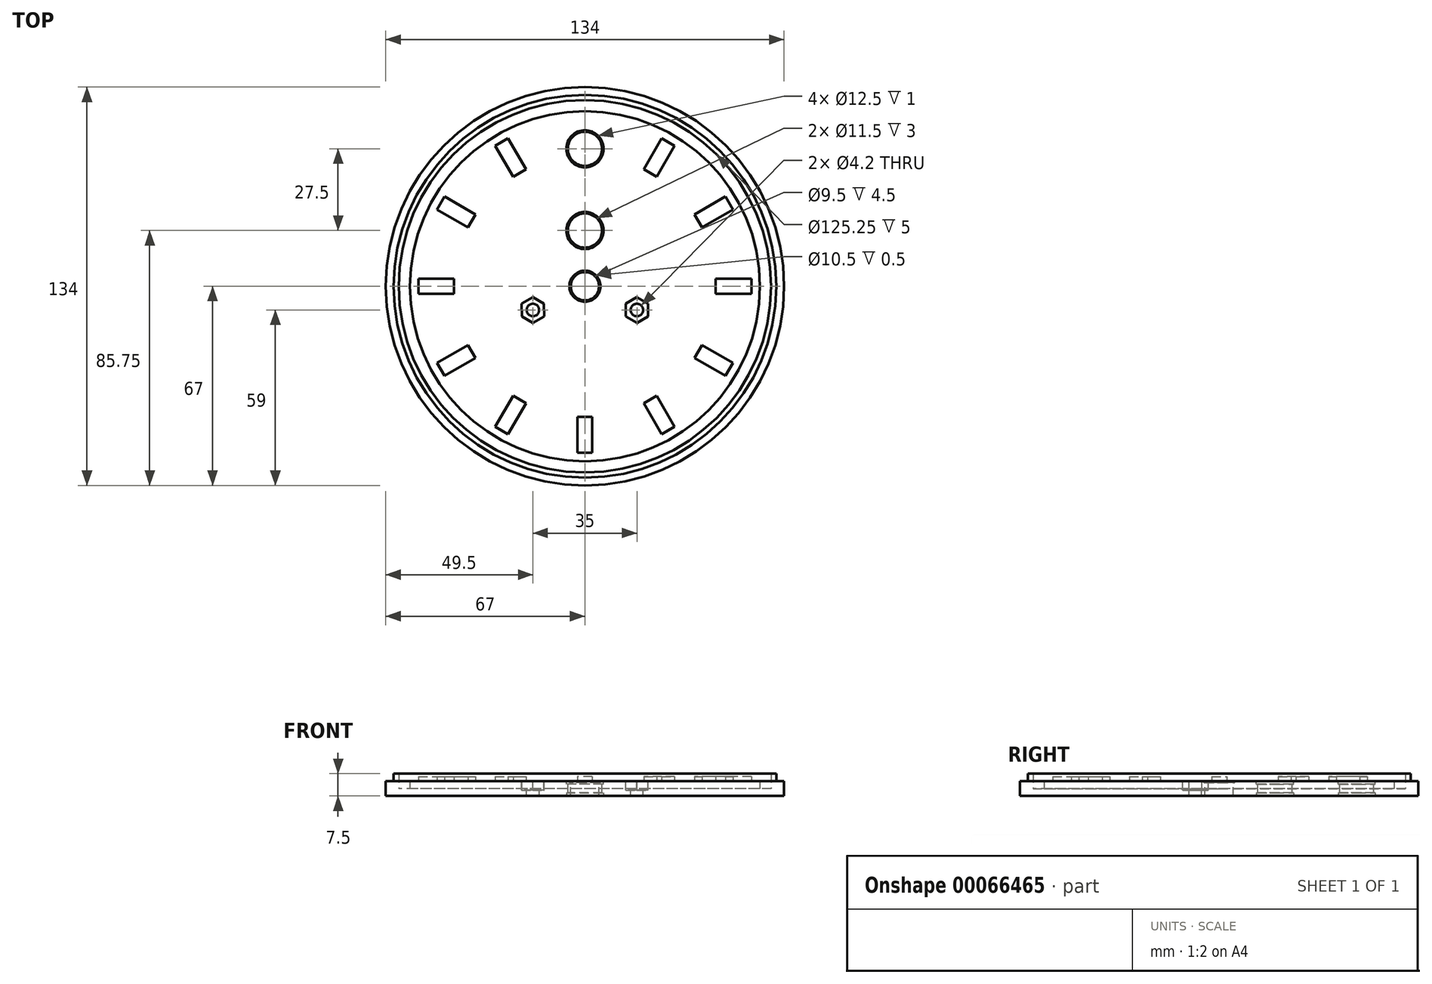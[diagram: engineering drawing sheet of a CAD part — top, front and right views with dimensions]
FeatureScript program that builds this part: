
annotation { "Feature Type Name" : "Feature", "Feature Type Description" : "" }
export const myFeature = defineFeature(function(context is Context, id is Id, definition is map)
    precondition{}
    {
        {
            var Q0;
            Q0=qCreatedBy(makeId("Top.planeOp"),FACE);
            var sketch = newSketch(context, id + "F0", { "sketchPlane" : qUnion([Q0])});
            skCircle(sketch, "E0", {"center": v(0, 0) * mm, "radius": 67 * mm});
            skSolve(sketch);
        }
        {
            var Q0;
            Q0 = qSketchRegion(id + "F0", true);
            extrude(context, id + "F1", {"entities" : qUnion([Q0]), "endBound" : BoundingType.SYMMETRIC, "depth" : 5 * mm});
        }
        {
            var Q0;
            Q0=qCreatedBy(makeId("Top.planeOp"),FACE);
            var sketch = newSketch(context, id + "F2", { "sketchPlane" : qUnion([Q0])});
            skCircle(sketch, "E1", {"center": v(0, 0) * mm, "radius": 64.38 * mm});
            skCircle(sketch, "E2", {"center": v(0, 0) * mm, "radius": 62.62 * mm});
            skCircle(sketch, "E3", {"center": v(0, 0) * mm, "radius": 58.88 * mm});
            skSolve(sketch);
        }
        {
            var Q0;
            Q0 = qSketchRegion(id + "F2", true);
            extrude(context, id + "F3", {"entities" : qUnion([Q0]), "operationType" : NewBodyOperationType.ADD, "depth" : 5 * mm});
        }
        {
            var Q0;
            Q0=qCreatedBy(makeId("Top.planeOp"),FACE);
            var sketch = newSketch(context, id + "F4", { "sketchPlane" : qUnion([Q0])});
            skCircle(sketch, "E4", {"center": v(0, 0) * mm, "radius": 58.88 * mm});
            skCircle(sketch, "E5", {"center": v(0, 0) * mm, "radius": 62.62 * mm});
            skSolve(sketch);
        }
        {
            var Q0;
            Q0 = qSketchRegion(id + "F4", true);
            extrude(context, id + "F5", {"entities" : qUnion([Q0]), "operationType" : NewBodyOperationType.REMOVE, "depth" : 5 * mm});
        }
        {
            var Q0;
            Q0=makeQuery(id+"F3.boolean.opBoolean","SPLIT",FACE,{"disambiguationData":[TD([makeQuery(id+"F3.opExtrude","SWEPT_FACE",FACE,{"disambiguationData":[OSD([sQuery(id+"F2.wireOp",EDGE,"E2")])]})])],"derivedFrom":makeQuery(id+"F1.opExtrude","CAP_FACE",FACE,{"disambiguationData":[OSD([sQuery(id+"F0.wireOp",EDGE,"E0")])],"isStart":false})});
            var sketch = newSketch(context, id + "F6", { "sketchPlane" : qUnion([Q0])});
            skCircle(sketch, "E6", {"center": v(0, 0) * mm, "radius": 4.75 * mm});
            skCircle(sketch, "E7", {"center": v(0, 18.75) * mm, "radius": 5.75 * mm});
            skCircle(sketch, "E8", {"center": v(0, 46.25) * mm, "radius": 5.75 * mm});
            skLineSegment(sketch, "E9", {"start": v(0, -8) * mm, "end": v(17.5, -8) * mm, "construction": true});
            skLineSegment(sketch, "E10", {"start": v(0, 0) * mm, "end": v(0, -8) * mm, "construction": true});
            skCircle(sketch, "E11", {"center": v(17.5, -8) * mm, "radius": 2.1 * mm});
            skCircle(sketch, "E12.MirrorC", {"center": v(-17.5, -8) * mm, "radius": 2.1 * mm});
            skSolve(sketch);
        }
        {
            var Q0;
            Q0 = qSketchRegion(id + "F6", true);
            extrude(context, id + "F7", {"entities" : qUnion([Q0]), "operationType" : NewBodyOperationType.REMOVE, "endBound" : BoundingType.THROUGH_ALL, "oppositeDirection" : true, "depth" : 25 * mm});
        }
        {
            var Q0;
            Q0=makeQuery(id+"F3.boolean.opBoolean","SPLIT",FACE,{"disambiguationData":[TD([makeQuery(id+"F3.opExtrude","SWEPT_FACE",FACE,{"disambiguationData":[OSD([sQuery(id+"F2.wireOp",EDGE,"E2")])]})])],"derivedFrom":makeQuery(id+"F1.opExtrude","CAP_FACE",FACE,{"disambiguationData":[OSD([sQuery(id+"F0.wireOp",EDGE,"E0")])],"isStart":false})});
            var sketch = newSketch(context, id + "F8", { "sketchPlane" : qUnion([Q0])});
            skCircle(sketch, "E13", {"center": v(0, 46.25) * mm, "radius": 6.25 * mm});
            skCircle(sketch, "E14", {"center": v(0, 18.75) * mm, "radius": 6.25 * mm});
            skCircle(sketch, "E15", {"center": v(0, 0) * mm, "radius": 5.25 * mm});
            skCircle(sketch, "E16.cCircle", {"center": v(17.5, -8) * mm, "radius": 3.75 * mm, "construction": true});
            skLineSegment(sketch, "E16.0", {"start": v(21.27, -10.14) * mm, "end": v(17.53, -12.33) * mm});
            skLineSegment(sketch, "E16.1", {"start": v(17.53, -12.33) * mm, "end": v(13.77, -10.2) * mm});
            skLineSegment(sketch, "E16.2", {"start": v(13.77, -10.2) * mm, "end": v(13.73, -5.86) * mm});
            skLineSegment(sketch, "E16.3", {"start": v(13.73, -5.86) * mm, "end": v(17.47, -3.67) * mm});
            skLineSegment(sketch, "E16.4", {"start": v(17.47, -3.67) * mm, "end": v(21.23, -5.8) * mm});
            skLineSegment(sketch, "E16.5", {"start": v(21.23, -5.8) * mm, "end": v(21.27, -10.14) * mm});
            skPoint(sketch, "E16.0.midPoint", {"position": v(19.4, -11.23) * mm});
            skCircle(sketch, "E17.cCircle", {"center": v(-17.5, -8) * mm, "radius": 3.75 * mm, "construction": true});
            skLineSegment(sketch, "E17.0", {"start": v(-13.73, -10.14) * mm, "end": v(-17.47, -12.33) * mm});
            skLineSegment(sketch, "E17.1", {"start": v(-17.47, -12.33) * mm, "end": v(-21.23, -10.2) * mm});
            skLineSegment(sketch, "E17.2", {"start": v(-21.23, -10.2) * mm, "end": v(-21.27, -5.86) * mm});
            skLineSegment(sketch, "E17.3", {"start": v(-21.27, -5.86) * mm, "end": v(-17.53, -3.67) * mm});
            skLineSegment(sketch, "E17.4", {"start": v(-17.53, -3.67) * mm, "end": v(-13.77, -5.8) * mm});
            skLineSegment(sketch, "E17.5", {"start": v(-13.77, -5.8) * mm, "end": v(-13.73, -10.14) * mm});
            skPoint(sketch, "E17.0.midPoint", {"position": v(-15.6, -11.23) * mm});
            skSolve(sketch);
        }
        {
            var Q0;
            Q0=makeQuery(id+"F8.imprint","IMPRINT",FACE,{"disambiguationData":[TD([[makeQuery(id+"F8.imprint","IMPRINT",EDGE,{"derivedFrom":sQuery(id+"F8.wireOp",EDGE,"E15")}),1.0]])]});
            extrude(context, id + "F9", {"entities" : qUnion([Q0]), "operationType" : NewBodyOperationType.REMOVE, "oppositeDirection" : true, "depth" : 0.5 * mm});
        }
        {
            var Q0;
            Q0=makeQuery(id+"F8.imprint","IMPRINT",FACE,{"disambiguationData":[TD([[makeQuery(id+"F8.imprint","IMPRINT",EDGE,{"derivedFrom":sQuery(id+"F8.wireOp",EDGE,"E14")}),1.0]])]});
            var Q1;
            Q1=makeQuery(id+"F8.imprint","IMPRINT",FACE,{"disambiguationData":[TD([[makeQuery(id+"F8.imprint","IMPRINT",EDGE,{"derivedFrom":sQuery(id+"F8.wireOp",EDGE,"E13")}),1.0]])]});
            extrude(context, id + "F10", {"entities" : qUnion([Q0, Q1]), "operationType" : NewBodyOperationType.REMOVE, "oppositeDirection" : true, "depth" : 1 * mm});
        }
        {
            var Q0;
            Q0=makeQuery(id+"F8.imprint","IMPRINT",FACE,{"disambiguationData":[TD([[makeQuery(id+"F8.imprint","IMPRINT",EDGE,{"derivedFrom":sQuery(id+"F8.wireOp",EDGE,"E16.0")}),-1.0]])]});
            var Q1;
            Q1=makeQuery(id+"F8.imprint","IMPRINT",FACE,{"disambiguationData":[TD([[makeQuery(id+"F8.imprint","IMPRINT",EDGE,{"derivedFrom":sQuery(id+"F8.wireOp",EDGE,"E17.0")}),-1.0]])]});
            extrude(context, id + "F11", {"entities" : qUnion([Q0, Q1]), "operationType" : NewBodyOperationType.REMOVE, "oppositeDirection" : true, "depth" : 3 * mm});
        }
        {
            var Q0;
            Q0=makeQuery(id+"F1.opExtrude","CAP_FACE",FACE,{"disambiguationData":[OSD([sQuery(id+"F0.wireOp",EDGE,"E0")])],"isStart":true});
            var sketch = newSketch(context, id + "F12", { "sketchPlane" : qUnion([Q0])});
            skCircle(sketch, "E18", {"center": v(0, -46.25) * mm, "radius": 6.25 * mm});
            skCircle(sketch, "E19", {"center": v(0, -18.75) * mm, "radius": 6.25 * mm});
            skSolve(sketch);
        }
        {
            var Q0;
            Q0=makeQuery(id+"F12.imprint","IMPRINT",FACE,{"disambiguationData":[TD([[makeQuery(id+"F12.imprint","IMPRINT",EDGE,{"derivedFrom":sQuery(id+"F12.wireOp",EDGE,"E18")}),1.0]])]});
            var Q1;
            Q1=makeQuery(id+"F12.imprint","IMPRINT",FACE,{"disambiguationData":[TD([[makeQuery(id+"F12.imprint","IMPRINT",EDGE,{"derivedFrom":sQuery(id+"F12.wireOp",EDGE,"E19")}),1.0]])]});
            extrude(context, id + "F13", {"entities" : qUnion([Q0, Q1]), "operationType" : NewBodyOperationType.REMOVE, "oppositeDirection" : true, "depth" : 1 * mm});
        }
        {
            var Q0;
            Q0=makeQuery(id+"F3.boolean.opBoolean","SPLIT",FACE,{"disambiguationData":[TD([makeQuery(id+"F3.opExtrude","SWEPT_FACE",FACE,{"disambiguationData":[OSD([sQuery(id+"F2.wireOp",EDGE,"E2")])]})])],"derivedFrom":makeQuery(id+"F1.opExtrude","CAP_FACE",FACE,{"disambiguationData":[OSD([sQuery(id+"F0.wireOp",EDGE,"E0")])],"isStart":false})});
            var sketch = newSketch(context, id + "F14", { "sketchPlane" : qUnion([Q0])});
            skCircle(sketch, "E20", {"center": v(0, 0) * mm, "radius": 50 * mm, "construction": true});
            skLineSegment(sketch, "E21.rect.bottom", {"start": v(2.5, -56) * mm, "end": v(-2.5, -56) * mm});
            skLineSegment(sketch, "E21.rect.top", {"start": v(2.5, -44) * mm, "end": v(-2.5, -44) * mm});
            skLineSegment(sketch, "E21.rect.left", {"start": v(2.5, -56) * mm, "end": v(2.5, -44) * mm});
            skLineSegment(sketch, "E21.rect.right", {"start": v(-2.5, -56) * mm, "end": v(-2.5, -44) * mm});
            skPoint(sketch, "E21.rect.middle", {"position": v(0, -50) * mm});
            skSolve(sketch);
        }
        {
            var Q0;
            Q0=makeQuery(id+"F14.imprint","IMPRINT",FACE,{"disambiguationData":[TD([[makeQuery(id+"F14.imprint","IMPRINT",EDGE,{"derivedFrom":sQuery(id+"F14.wireOp",EDGE,"E21.rect.bottom")}),-1.0]])]});
            extrude(context, id + "F15", {"entities" : qUnion([Q0]), "operationType" : NewBodyOperationType.ADD, "depth" : 1.5 * mm});
        }
        {
            var Q0;
            Q0=makeQuery(id+"F1.opExtrude","SWEPT_BODY",BODY,{"disambiguationData":[OSD([sQuery(id+"F0.wireOp",EDGE,"E0")])]});
            var Q1;
            Q1=makeQuery(id+"F15.opExtrude","CAP_FACE",FACE,{"disambiguationData":[OSD([sQuery(id+"F14.wireOp",EDGE,"E21.rect.bottom"),sQuery(id+"F14.wireOp",EDGE,"E21.rect.top"),sQuery(id+"F14.wireOp",EDGE,"E21.rect.left"),sQuery(id+"F14.wireOp",EDGE,"E21.rect.right")])],"isStart":false});
            var Q2;
            Q2=makeQuery(id+"F15.opExtrude","SWEPT_FACE",FACE,{"disambiguationData":[OSD([sQuery(id+"F14.wireOp",EDGE,"E21.rect.left")])]});
            var Q3;
            Q3=makeQuery(id+"F15.opExtrude","SWEPT_FACE",FACE,{"disambiguationData":[OSD([sQuery(id+"F14.wireOp",EDGE,"E21.rect.top")])]});
            var Q4;
            Q4=makeQuery(id+"F15.opExtrude","SWEPT_FACE",FACE,{"disambiguationData":[OSD([sQuery(id+"F14.wireOp",EDGE,"E21.rect.right")])]});
            var Q5;
            Q5=makeQuery(id+"F15.opExtrude","SWEPT_FACE",FACE,{"disambiguationData":[OSD([sQuery(id+"F14.wireOp",EDGE,"E21.rect.bottom")])]});
            var Q6;
            Q6=makeQuery(id+"F5.boolean.opBoolean","INTERSECT",EDGE,{"derivedFrom":[makeQuery(id+"F3.boolean.opBoolean","SPLIT",FACE,{"disambiguationData":[TD([makeQuery(id+"F3.opExtrude","SWEPT_FACE",FACE,{"disambiguationData":[OSD([sQuery(id+"F2.wireOp",EDGE,"E2")])]})])],"derivedFrom":makeQuery(id+"F1.opExtrude","CAP_FACE",FACE,{"disambiguationData":[OSD([sQuery(id+"F0.wireOp",EDGE,"E0")])],"isStart":false})}),makeQuery(id+"F5.opExtrude","SWEPT_FACE",FACE,{"disambiguationData":[OSD([sQuery(id+"F4.wireOp",EDGE,"E4")])]})]});
            circularPattern(context, id + "F16", {"operationType" : NewBodyOperationType.ADD, "faces" : qUnion([Q1, Q2, Q3, Q4, Q5]), "axis" : qUnion([Q6]), "angle" : 30 * degree, "instanceCount" : 6, "patternType" : PatternType.FACE});
        }
        {
            var Q0;
            Q0=makeQuery(id+"F15.opExtrude","CAP_FACE",FACE,{"disambiguationData":[OSD([sQuery(id+"F14.wireOp",EDGE,"E21.rect.bottom"),sQuery(id+"F14.wireOp",EDGE,"E21.rect.top"),sQuery(id+"F14.wireOp",EDGE,"E21.rect.left"),sQuery(id+"F14.wireOp",EDGE,"E21.rect.right")])],"isStart":false});
            var Q1;
            Q1=makeQuery(id+"F15.opExtrude","SWEPT_FACE",FACE,{"disambiguationData":[OSD([sQuery(id+"F14.wireOp",EDGE,"E21.rect.left")])]});
            var Q2;
            Q2=makeQuery(id+"F15.opExtrude","SWEPT_FACE",FACE,{"disambiguationData":[OSD([sQuery(id+"F14.wireOp",EDGE,"E21.rect.bottom")])]});
            var Q3;
            Q3=makeQuery(id+"F15.opExtrude","SWEPT_FACE",FACE,{"disambiguationData":[OSD([sQuery(id+"F14.wireOp",EDGE,"E21.rect.right")])]});
            var Q4;
            Q4=makeQuery(id+"F15.opExtrude","SWEPT_FACE",FACE,{"disambiguationData":[OSD([sQuery(id+"F14.wireOp",EDGE,"E21.rect.top")])]});
            var Q5;
            Q5=makeQuery(id+"F5.boolean.opBoolean","INTERSECT",EDGE,{"derivedFrom":[makeQuery(id+"F3.boolean.opBoolean","SPLIT",FACE,{"disambiguationData":[TD([makeQuery(id+"F3.opExtrude","SWEPT_FACE",FACE,{"disambiguationData":[OSD([sQuery(id+"F2.wireOp",EDGE,"E2")])]})])],"derivedFrom":makeQuery(id+"F1.opExtrude","CAP_FACE",FACE,{"disambiguationData":[OSD([sQuery(id+"F0.wireOp",EDGE,"E0")])],"isStart":false})}),makeQuery(id+"F5.opExtrude","SWEPT_FACE",FACE,{"disambiguationData":[OSD([sQuery(id+"F4.wireOp",EDGE,"E4")])]})]});
            circularPattern(context, id + "F17", {"faces" : qUnion([Q0, Q1, Q2, Q3, Q4]), "axis" : qUnion([Q5]), "angle" : 30 * degree, "instanceCount" : 6, "oppositeDirection" : true, "patternType" : PatternType.FACE});
        }
    });
